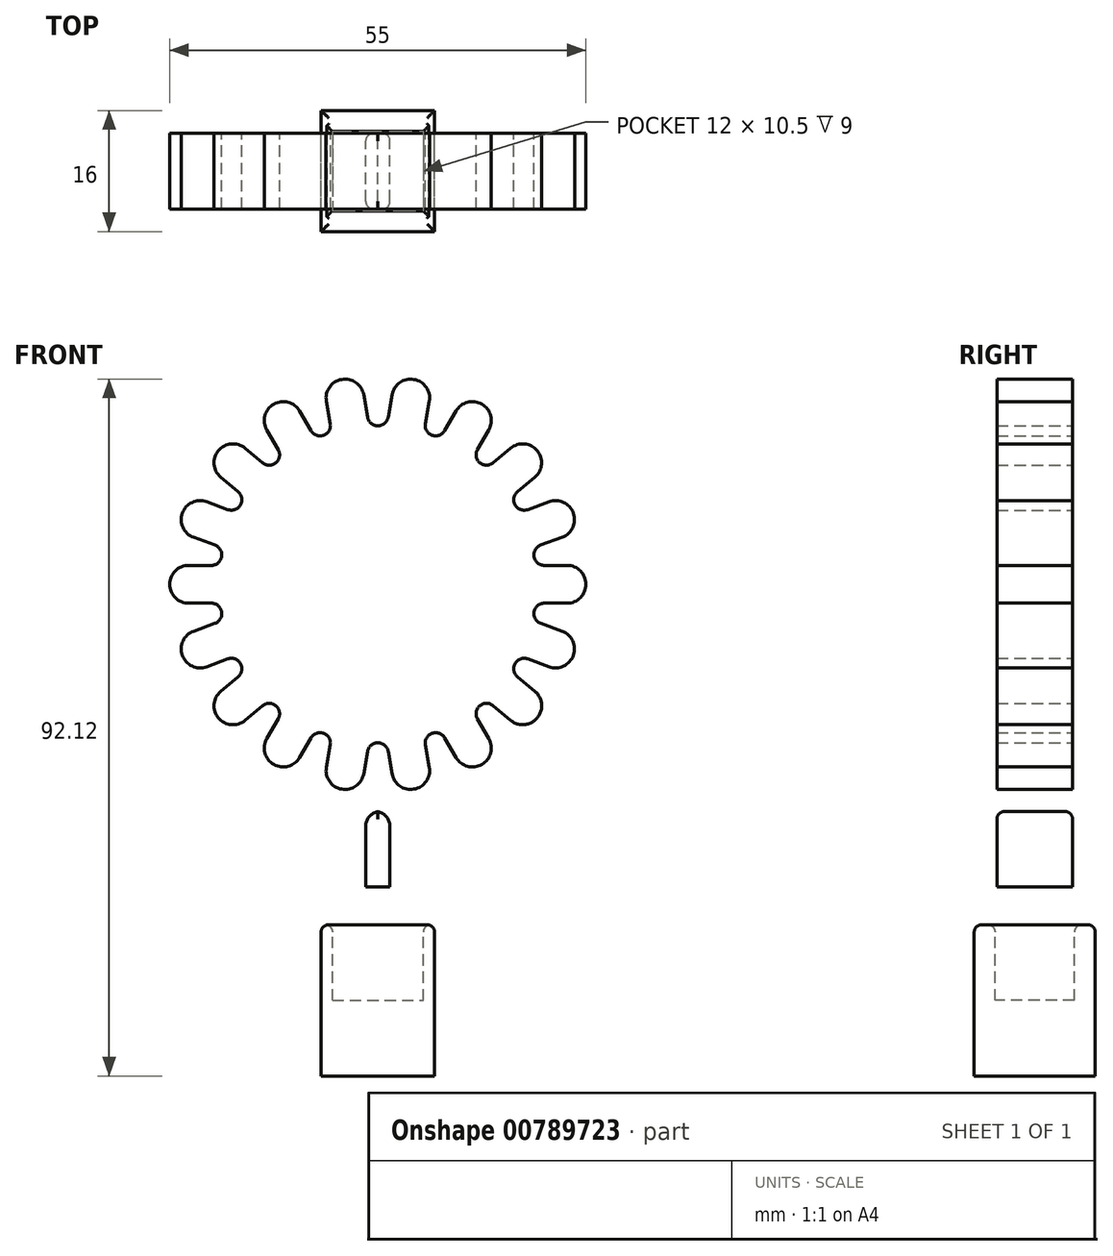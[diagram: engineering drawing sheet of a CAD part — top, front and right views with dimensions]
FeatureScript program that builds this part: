
annotation { "Feature Type Name" : "Feature", "Feature Type Description" : "" }
export const myFeature = defineFeature(function(context is Context, id is Id, definition is map)
    precondition{}
    {
        {
            var Q0;
            Q0=qCreatedBy(makeId("Front.planeOp"),FACE);
            var sketch = newSketch(context, id + "F0", { "sketchPlane" : qUnion([Q0])});
            skLineSegment(sketch, "E0", {"start": v(0, 0) * mm, "end": v(-40.76, 0) * mm, "construction": true});
            skLineSegment(sketch, "E1", {"start": v(-22, 2.5) * mm, "end": v(-25, 2.5) * mm});
            skLineSegment(sketch, "E2.MirrorCS", {"start": v(-22, -2.5) * mm, "end": v(-25, -2.5) * mm});
            skArc(sketch, "E3", {"start": v(-25, 2.5) * mm, "mid": v(-27.5, 0) * mm, "end": v(-25, -2.5) * mm});
            skLineSegment(sketch, "E4.1.0", {"start": v(-21.53, -5.18) * mm, "end": v(-24.35, -6.2) * mm});
            skArc(sketch, "E4.1.1", {"start": v(-24.35, -6.2) * mm, "mid": v(-25.84, -9.4) * mm, "end": v(-22.64, -10.9) * mm});
            skLineSegment(sketch, "E4.1.2", {"start": v(-19.82, -9.87) * mm, "end": v(-22.64, -10.9) * mm});
            skLineSegment(sketch, "E4.2.0", {"start": v(-18.46, -12.23) * mm, "end": v(-20.76, -14.15) * mm});
            skArc(sketch, "E4.2.1", {"start": v(-20.76, -14.15) * mm, "mid": v(-21.07, -17.68) * mm, "end": v(-17.54, -17.98) * mm});
            skLineSegment(sketch, "E4.2.2", {"start": v(-15.25, -16.06) * mm, "end": v(-17.54, -17.98) * mm});
            skLineSegment(sketch, "E4.3.0", {"start": v(-13.17, -17.8) * mm, "end": v(-14.67, -20.4) * mm});
            skArc(sketch, "E4.3.1", {"start": v(-14.67, -20.4) * mm, "mid": v(-13.75, -23.82) * mm, "end": v(-10.33, -22.9) * mm});
            skLineSegment(sketch, "E4.3.2", {"start": v(-8.83, -20.3) * mm, "end": v(-10.33, -22.9) * mm});
            skLineSegment(sketch, "E4.4.0", {"start": v(-6.28, -21.23) * mm, "end": v(-6.8, -24.19) * mm});
            skArc(sketch, "E4.4.1", {"start": v(-6.8, -24.19) * mm, "mid": v(-4.78, -27.08) * mm, "end": v(-1.88, -25.05) * mm});
            skLineSegment(sketch, "E4.4.2", {"start": v(-1.36, -22.1) * mm, "end": v(-1.88, -25.05) * mm});
            skLineSegment(sketch, "E4.5.0", {"start": v(1.36, -22.1) * mm, "end": v(1.88, -25.05) * mm});
            skArc(sketch, "E4.5.1", {"start": v(1.88, -25.05) * mm, "mid": v(4.78, -27.08) * mm, "end": v(6.8, -24.19) * mm});
            skLineSegment(sketch, "E4.5.2", {"start": v(6.28, -21.23) * mm, "end": v(6.8, -24.19) * mm});
            skLineSegment(sketch, "E4.6.0", {"start": v(8.83, -20.3) * mm, "end": v(10.33, -22.9) * mm});
            skArc(sketch, "E4.6.1", {"start": v(10.33, -22.9) * mm, "mid": v(13.75, -23.82) * mm, "end": v(14.67, -20.4) * mm});
            skLineSegment(sketch, "E4.6.2", {"start": v(13.17, -17.8) * mm, "end": v(14.67, -20.4) * mm});
            skLineSegment(sketch, "E4.7.0", {"start": v(15.25, -16.06) * mm, "end": v(17.54, -17.98) * mm});
            skArc(sketch, "E4.7.1", {"start": v(17.54, -17.98) * mm, "mid": v(21.07, -17.68) * mm, "end": v(20.76, -14.15) * mm});
            skLineSegment(sketch, "E4.7.2", {"start": v(18.46, -12.23) * mm, "end": v(20.76, -14.15) * mm});
            skLineSegment(sketch, "E4.8.0", {"start": v(19.82, -9.87) * mm, "end": v(22.64, -10.9) * mm});
            skArc(sketch, "E4.8.1", {"start": v(22.64, -10.9) * mm, "mid": v(25.84, -9.4) * mm, "end": v(24.35, -6.2) * mm});
            skLineSegment(sketch, "E4.8.2", {"start": v(21.53, -5.18) * mm, "end": v(24.35, -6.2) * mm});
            skLineSegment(sketch, "E4.9.0", {"start": v(22, -2.5) * mm, "end": v(25, -2.5) * mm});
            skArc(sketch, "E4.9.1", {"start": v(25, -2.5) * mm, "mid": v(27.5, 0) * mm, "end": v(25, 2.5) * mm});
            skLineSegment(sketch, "E4.9.2", {"start": v(22, 2.5) * mm, "end": v(25, 2.5) * mm});
            skLineSegment(sketch, "E4.10.0", {"start": v(21.53, 5.18) * mm, "end": v(24.35, 6.2) * mm});
            skArc(sketch, "E4.10.1", {"start": v(24.35, 6.2) * mm, "mid": v(25.84, 9.4) * mm, "end": v(22.64, 10.9) * mm});
            skLineSegment(sketch, "E4.10.2", {"start": v(19.82, 9.87) * mm, "end": v(22.64, 10.9) * mm});
            skLineSegment(sketch, "E4.11.0", {"start": v(18.46, 12.23) * mm, "end": v(20.76, 14.15) * mm});
            skArc(sketch, "E4.11.1", {"start": v(20.76, 14.15) * mm, "mid": v(21.07, 17.68) * mm, "end": v(17.54, 17.98) * mm});
            skLineSegment(sketch, "E4.11.2", {"start": v(15.25, 16.06) * mm, "end": v(17.54, 17.98) * mm});
            skLineSegment(sketch, "E4.12.0", {"start": v(13.17, 17.8) * mm, "end": v(14.67, 20.4) * mm});
            skArc(sketch, "E4.12.1", {"start": v(14.67, 20.4) * mm, "mid": v(13.75, 23.82) * mm, "end": v(10.33, 22.9) * mm});
            skLineSegment(sketch, "E4.12.2", {"start": v(8.83, 20.3) * mm, "end": v(10.33, 22.9) * mm});
            skLineSegment(sketch, "E4.13.0", {"start": v(6.28, 21.23) * mm, "end": v(6.8, 24.19) * mm});
            skArc(sketch, "E4.13.1", {"start": v(6.8, 24.19) * mm, "mid": v(4.78, 27.08) * mm, "end": v(1.88, 25.05) * mm});
            skLineSegment(sketch, "E4.13.2", {"start": v(1.36, 22.1) * mm, "end": v(1.88, 25.05) * mm});
            skLineSegment(sketch, "E4.14.0", {"start": v(-1.36, 22.1) * mm, "end": v(-1.88, 25.05) * mm});
            skArc(sketch, "E4.14.1", {"start": v(-1.88, 25.05) * mm, "mid": v(-4.78, 27.08) * mm, "end": v(-6.8, 24.19) * mm});
            skLineSegment(sketch, "E4.14.2", {"start": v(-6.28, 21.23) * mm, "end": v(-6.8, 24.19) * mm});
            skLineSegment(sketch, "E4.15.0", {"start": v(-8.83, 20.3) * mm, "end": v(-10.33, 22.9) * mm});
            skArc(sketch, "E4.15.1", {"start": v(-10.33, 22.9) * mm, "mid": v(-13.75, 23.82) * mm, "end": v(-14.67, 20.4) * mm});
            skLineSegment(sketch, "E4.15.2", {"start": v(-13.17, 17.8) * mm, "end": v(-14.67, 20.4) * mm});
            skLineSegment(sketch, "E4.16.0", {"start": v(-15.25, 16.06) * mm, "end": v(-17.54, 17.98) * mm});
            skArc(sketch, "E4.16.1", {"start": v(-17.54, 17.98) * mm, "mid": v(-21.07, 17.68) * mm, "end": v(-20.76, 14.15) * mm});
            skLineSegment(sketch, "E4.16.2", {"start": v(-18.46, 12.23) * mm, "end": v(-20.76, 14.15) * mm});
            skLineSegment(sketch, "E4.17.0", {"start": v(-19.82, 9.87) * mm, "end": v(-22.64, 10.9) * mm});
            skArc(sketch, "E4.17.1", {"start": v(-22.64, 10.9) * mm, "mid": v(-25.84, 9.4) * mm, "end": v(-24.35, 6.2) * mm});
            skLineSegment(sketch, "E4.17.2", {"start": v(-21.53, 5.18) * mm, "end": v(-24.35, 6.2) * mm});
            skPoint(sketch, "E4.center", {"position": v(0, 0) * mm});
            skArc(sketch, "E5", {"start": v(-22, 2.5) * mm, "mid": v(-20.64, 3.64) * mm, "end": v(-21.53, 5.18) * mm});
            skArc(sketch, "E6.1.0", {"start": v(-21.53, -5.18) * mm, "mid": v(-20.64, -3.64) * mm, "end": v(-22, -2.5) * mm});
            skArc(sketch, "E6.2.0", {"start": v(-18.46, -12.23) * mm, "mid": v(-18.15, -10.48) * mm, "end": v(-19.82, -9.87) * mm});
            skArc(sketch, "E6.3.0", {"start": v(-13.17, -17.8) * mm, "mid": v(-13.47, -16.06) * mm, "end": v(-15.25, -16.06) * mm});
            skArc(sketch, "E6.4.0", {"start": v(-6.28, -21.23) * mm, "mid": v(-7.17, -19.7) * mm, "end": v(-8.83, -20.3) * mm});
            skArc(sketch, "E6.5.0", {"start": v(1.36, -22.1) * mm, "mid": v(0, -20.96) * mm, "end": v(-1.36, -22.1) * mm});
            skArc(sketch, "E6.6.0", {"start": v(8.83, -20.3) * mm, "mid": v(7.17, -19.7) * mm, "end": v(6.28, -21.23) * mm});
            skArc(sketch, "E6.7.0", {"start": v(15.25, -16.06) * mm, "mid": v(13.47, -16.06) * mm, "end": v(13.17, -17.8) * mm});
            skArc(sketch, "E6.8.0", {"start": v(19.82, -9.87) * mm, "mid": v(18.15, -10.48) * mm, "end": v(18.46, -12.23) * mm});
            skArc(sketch, "E6.9.0", {"start": v(22, -2.5) * mm, "mid": v(20.64, -3.64) * mm, "end": v(21.53, -5.18) * mm});
            skArc(sketch, "E6.10.0", {"start": v(21.53, 5.18) * mm, "mid": v(20.64, 3.64) * mm, "end": v(22, 2.5) * mm});
            skArc(sketch, "E6.11.0", {"start": v(18.46, 12.23) * mm, "mid": v(18.15, 10.48) * mm, "end": v(19.82, 9.87) * mm});
            skArc(sketch, "E6.12.0", {"start": v(13.17, 17.8) * mm, "mid": v(13.47, 16.06) * mm, "end": v(15.25, 16.06) * mm});
            skArc(sketch, "E6.13.0", {"start": v(6.28, 21.23) * mm, "mid": v(7.17, 19.7) * mm, "end": v(8.83, 20.3) * mm});
            skArc(sketch, "E6.14.0", {"start": v(-1.36, 22.1) * mm, "mid": v(0, 20.96) * mm, "end": v(1.36, 22.1) * mm});
            skArc(sketch, "E6.15.0", {"start": v(-8.83, 20.3) * mm, "mid": v(-7.17, 19.7) * mm, "end": v(-6.28, 21.23) * mm});
            skArc(sketch, "E6.16.0", {"start": v(-15.25, 16.06) * mm, "mid": v(-13.47, 16.06) * mm, "end": v(-13.17, 17.8) * mm});
            skArc(sketch, "E6.17.0", {"start": v(-19.82, 9.87) * mm, "mid": v(-18.15, 10.48) * mm, "end": v(-18.46, 12.23) * mm});
            skSolve(sketch);
        }
        {
            var Q0;
            Q0=makeQuery(id+"F0.imprint","IMPRINT",FACE,{"disambiguationData":[TD([[makeQuery(id+"F0.imprint","IMPRINT",EDGE,{"derivedFrom":sQuery(id+"F0.wireOp",EDGE,"E1")}),1.0]])]});
            extrude(context, id + "F1", {"entities" : qUnion([Q0]), "depth" : 5 * mm, "offsetDistance" : 25 * mm, "hasSecondDirection" : true, "secondDirectionOppositeDirection" : true, "secondDirectionDepth" : 5 * mm});
        }
        {
            var Q0;
            Q0=qCreatedBy(makeId("Front.planeOp"),FACE);
            var sketch = newSketch(context, id + "F2", { "sketchPlane" : qUnion([Q0])});
            skLineSegment(sketch, "E7", {"start": v(-1.6, -40) * mm, "end": v(-1.6, -30) * mm});
            skLineSegment(sketch, "E8", {"start": v(-1.6, -30) * mm, "end": v(1.6, -30) * mm});
            skLineSegment(sketch, "E9", {"start": v(1.6, -30) * mm, "end": v(1.6, -40) * mm});
            skLineSegment(sketch, "E10", {"start": v(0, 0) * mm, "end": v(0, -30) * mm, "construction": true});
            skLineSegment(sketch, "E11", {"start": v(-1.6, -40) * mm, "end": v(1.6, -40) * mm});
            skSolve(sketch);
        }
        {
            var Q0;
            Q0=makeQuery(id+"F2.imprint","IMPRINT",FACE,{"disambiguationData":[TD([[makeQuery(id+"F2.imprint","IMPRINT",EDGE,{"derivedFrom":sQuery(id+"F2.wireOp",EDGE,"E7")}),-1.0]])]});
            extrude(context, id + "F3", {"entities" : qUnion([Q0]), "depth" : 5 * mm, "offsetDistance" : 25 * mm, "hasSecondDirection" : true, "secondDirectionOppositeDirection" : true, "secondDirectionDepth" : 5 * mm});
        }
        {
            var Q0;
            Q0=makeQuery(id+"F3.opExtrude","SWEPT_EDGE",EDGE,{"disambiguationData":[OSD([sQuery(id+"F2.wireOp",EDGE,"E7"),sQuery(id+"F2.wireOp",EDGE,"E8")])]});
            var Q1;
            Q1=makeQuery(id+"F3.opExtrude","SWEPT_EDGE",EDGE,{"disambiguationData":[OSD([sQuery(id+"F2.wireOp",EDGE,"E8"),sQuery(id+"F2.wireOp",EDGE,"E9")])]});
            fillet(context, id + "F4", {"entities" : qUnion([Q0, Q1]), "radius" : 2 * mm, "tangentPropagation" : true, "allowEdgeOverflow" : false});
        }
        {
            var Q0;
            {var subQ0=sQuery(id+"F2.wireOp",EDGE,"E9");var subQ1=sQuery(id+"F2.wireOp",EDGE,"E8");Q0=makeQuery(id+"F4.opFillet","BLEND_EDGE",EDGE,{"blendedFrom":[makeQuery(id+"F3.opExtrude","SWEPT_EDGE",EDGE,{"disambiguationData":[OSD([subQ1,subQ0])]}),makeQuery(id+"F3.opExtrude","CAP_FACE",FACE,{"disambiguationData":[OSD([sQuery(id+"F2.wireOp",EDGE,"E7"),subQ1,subQ0,sQuery(id+"F2.wireOp",EDGE,"E11")])],"isStart":false})],"blendedInto":[makeQuery(id+"F3.opExtrude","CAP_FACE",FACE,{"disambiguationData":[OSD([sQuery(id+"F2.wireOp",EDGE,"E7"),subQ1,subQ0,sQuery(id+"F2.wireOp",EDGE,"E11")])],"isStart":false})]});}
            var Q1;
            {var subQ0=sQuery(id+"F2.wireOp",EDGE,"E8");var subQ1=sQuery(id+"F2.wireOp",EDGE,"E7");Q1=makeQuery(id+"F4.opFillet","BLEND_EDGE",EDGE,{"blendedFrom":[makeQuery(id+"F3.opExtrude","SWEPT_EDGE",EDGE,{"disambiguationData":[OSD([subQ1,subQ0])]}),makeQuery(id+"F3.opExtrude","CAP_FACE",FACE,{"disambiguationData":[OSD([subQ1,subQ0,sQuery(id+"F2.wireOp",EDGE,"E9"),sQuery(id+"F2.wireOp",EDGE,"E11")])],"isStart":false})],"blendedInto":[makeQuery(id+"F3.opExtrude","CAP_FACE",FACE,{"disambiguationData":[OSD([subQ1,subQ0,sQuery(id+"F2.wireOp",EDGE,"E9"),sQuery(id+"F2.wireOp",EDGE,"E11")])],"isStart":false})]});}
            var Q2;
            {var subQ0=sQuery(id+"F2.wireOp",EDGE,"E9");var subQ1=sQuery(id+"F2.wireOp",EDGE,"E8");Q2=makeQuery(id+"F4.opFillet","BLEND_EDGE",EDGE,{"blendedFrom":[makeQuery(id+"F3.opExtrude","SWEPT_EDGE",EDGE,{"disambiguationData":[OSD([subQ1,subQ0])]}),makeQuery(id+"F3.opExtrude","CAP_FACE",FACE,{"disambiguationData":[OSD([sQuery(id+"F2.wireOp",EDGE,"E7"),subQ1,subQ0,sQuery(id+"F2.wireOp",EDGE,"E11")])],"isStart":true})],"blendedInto":[makeQuery(id+"F3.opExtrude","CAP_FACE",FACE,{"disambiguationData":[OSD([sQuery(id+"F2.wireOp",EDGE,"E7"),subQ1,subQ0,sQuery(id+"F2.wireOp",EDGE,"E11")])],"isStart":true})]});}
            var Q3;
            {var subQ0=sQuery(id+"F2.wireOp",EDGE,"E8");var subQ1=sQuery(id+"F2.wireOp",EDGE,"E7");Q3=makeQuery(id+"F4.opFillet","BLEND_EDGE",EDGE,{"blendedFrom":[makeQuery(id+"F3.opExtrude","SWEPT_EDGE",EDGE,{"disambiguationData":[OSD([subQ1,subQ0])]}),makeQuery(id+"F3.opExtrude","CAP_FACE",FACE,{"disambiguationData":[OSD([subQ1,subQ0,sQuery(id+"F2.wireOp",EDGE,"E9"),sQuery(id+"F2.wireOp",EDGE,"E11")])],"isStart":true})],"blendedInto":[makeQuery(id+"F3.opExtrude","CAP_FACE",FACE,{"disambiguationData":[OSD([subQ1,subQ0,sQuery(id+"F2.wireOp",EDGE,"E9"),sQuery(id+"F2.wireOp",EDGE,"E11")])],"isStart":true})]});}
            fillet(context, id + "F5", {"entities" : qUnion([Q0, Q1, Q2, Q3]), "radius" : 1 * mm, "tangentPropagation" : true, "allowEdgeOverflow" : false});
        }
        {
            var Q0;
            Q0=qCreatedBy(makeId("Front.planeOp"),FACE);
            var sketch = newSketch(context, id + "F6", { "sketchPlane" : qUnion([Q0])});
            skLineSegment(sketch, "E12.bottom", {"start": v(-7.5, -45) * mm, "end": v(7.5, -45) * mm});
            skLineSegment(sketch, "E12.top", {"start": v(-7.5, -65) * mm, "end": v(7.5, -65) * mm});
            skLineSegment(sketch, "E12.left", {"start": v(-7.5, -45) * mm, "end": v(-7.5, -65) * mm});
            skLineSegment(sketch, "E12.right", {"start": v(7.5, -45) * mm, "end": v(7.5, -65) * mm});
            skLineSegment(sketch, "E13", {"start": v(0, 0) * mm, "end": v(0, -45) * mm, "construction": true});
            skSolve(sketch);
        }
        {
            var Q0;
            Q0=makeQuery(id+"F6.imprint","IMPRINT",FACE,{"disambiguationData":[TD([[makeQuery(id+"F6.imprint","IMPRINT",EDGE,{"derivedFrom":sQuery(id+"F6.wireOp",EDGE,"E12.bottom")}),-1.0]])]});
            extrude(context, id + "F7", {"entities" : qUnion([Q0]), "depth" : 8 * mm, "offsetDistance" : 25 * mm, "hasSecondDirection" : true, "secondDirectionOppositeDirection" : true, "secondDirectionDepth" : 8 * mm});
        }
        {
            var Q0;
            Q0=makeQuery(id+"F7.opExtrude","SWEPT_FACE",FACE,{"disambiguationData":[OSD([sQuery(id+"F6.wireOp",EDGE,"E12.bottom")])]});
            var sketch = newSketch(context, id + "F8", { "sketchPlane" : qUnion([Q0])});
            skLineSegment(sketch, "E14.bottom", {"start": v(-6, 5.25) * mm, "end": v(6, 5.25) * mm});
            skLineSegment(sketch, "E14.top", {"start": v(-6, -5.25) * mm, "end": v(6, -5.25) * mm});
            skLineSegment(sketch, "E14.left", {"start": v(-6, 5.25) * mm, "end": v(-6, -5.25) * mm});
            skLineSegment(sketch, "E14.right", {"start": v(6, 5.25) * mm, "end": v(6, -5.25) * mm});
            skPoint(sketch, "E14.middle", {"position": v(0, 0) * mm});
            skSolve(sketch);
        }
        {
            var Q0;
            Q0=makeQuery(id+"F8.imprint","IMPRINT",FACE,{"disambiguationData":[TD([[makeQuery(id+"F8.imprint","IMPRINT",EDGE,{"derivedFrom":sQuery(id+"F8.wireOp",EDGE,"E14.bottom")}),-1.0]])]});
            extrude(context, id + "F9", {"entities" : qUnion([Q0]), "operationType" : NewBodyOperationType.REMOVE, "oppositeDirection" : true, "depth" : 10 * mm, "offsetDistance" : 25 * mm});
        }
        {
            var Q0;
            Q0=makeQuery(id+"F7.opExtrude","SWEPT_FACE",FACE,{"disambiguationData":[OSD([sQuery(id+"F6.wireOp",EDGE,"E12.bottom")])]});
            fillet(context, id + "F10", {"entities" : qUnion([Q0]), "radius" : 1 * mm, "tangentPropagation" : true, "allowEdgeOverflow" : false});
        }
    });
